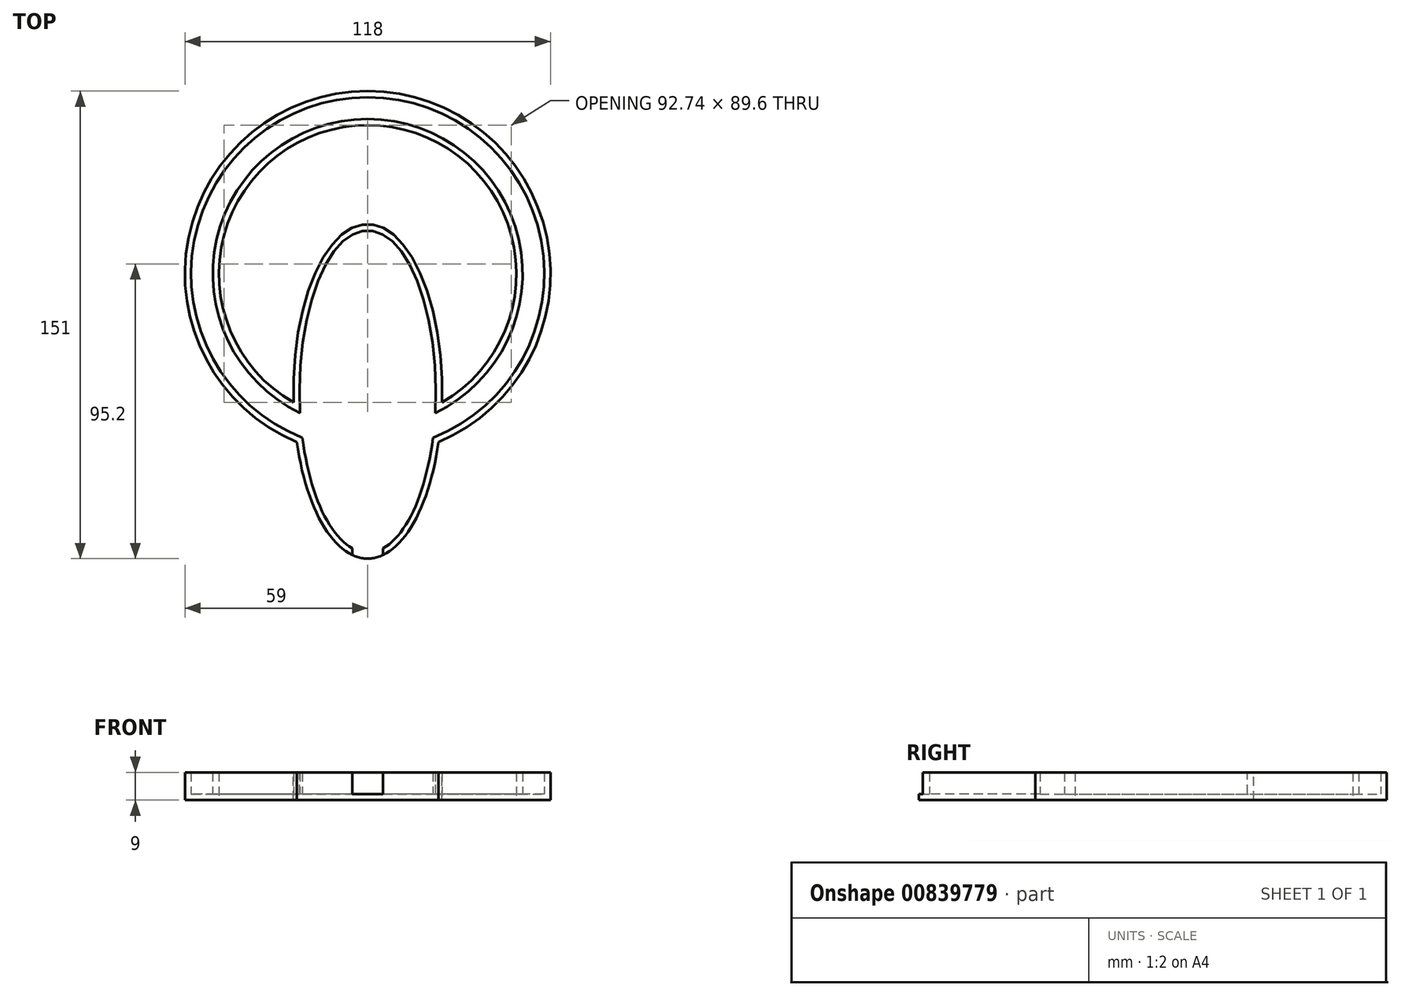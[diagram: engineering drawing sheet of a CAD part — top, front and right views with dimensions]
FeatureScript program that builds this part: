
annotation { "Feature Type Name" : "Feature", "Feature Type Description" : "" }
export const myFeature = defineFeature(function(context is Context, id is Id, definition is map)
    precondition{}
    {
        {
            var Q0;
            Q0=qCreatedBy(makeId("Top.planeOp"),FACE);
            var sketch = newSketch(context, id + "F0", { "sketchPlane" : qUnion([Q0])});
            skCircle(sketch, "E0", {"center": v(0, 0) * mm, "radius": 48 * mm});
            skCircle(sketch, "E1", {"center": v(0, 0) * mm, "radius": 50 * mm});
            skSolve(sketch);
        }
        {
            var Q0;
            Q0=makeQuery(id+"F0.imprint","IMPRINT",FACE,{"disambiguationData":[TD([[makeQuery(id+"F0.imprint","IMPRINT",EDGE,{"derivedFrom":sQuery(id+"F0.wireOp",EDGE,"E0")}),-1.0]])]});
            extrude(context, id + "F1", {"entities" : qUnion([Q0]), "depth" : 9 * mm, "offsetDistance" : 25 * mm});
        }
        {
            var Q0;
            Q0=qCreatedBy(makeId("Top.planeOp"),FACE);
            var sketch = newSketch(context, id + "F2", { "sketchPlane" : qUnion([Q0])});
            skCircle(sketch, "E2", {"center": v(0, 0) * mm, "radius": 50 * mm});
            skCircle(sketch, "E3", {"center": v(0, 0) * mm, "radius": 57 * mm});
            skSolve(sketch);
        }
        {
            var Q0;
            Q0=makeQuery(id+"F2.imprint","IMPRINT",FACE,{"disambiguationData":[TD([[makeQuery(id+"F2.imprint","IMPRINT",EDGE,{"derivedFrom":sQuery(id+"F2.wireOp",EDGE,"E2")}),-1.0]])]});
            extrude(context, id + "F3", {"entities" : qUnion([Q0]), "operationType" : NewBodyOperationType.ADD, "depth" : 2 * mm, "offsetDistance" : 25 * mm});
        }
        {
            var Q0;
            Q0=qCreatedBy(makeId("Top.planeOp"),FACE);
            var sketch = newSketch(context, id + "F4", { "sketchPlane" : qUnion([Q0])});
            skCircle(sketch, "E4", {"center": v(0, 0) * mm, "radius": 57 * mm});
            skCircle(sketch, "E5", {"center": v(0, 0) * mm, "radius": 59 * mm});
            skSolve(sketch);
        }
        {
            var Q0;
            Q0=makeQuery(id+"F4.imprint","IMPRINT",FACE,{"disambiguationData":[TD([[makeQuery(id+"F4.imprint","IMPRINT",EDGE,{"derivedFrom":sQuery(id+"F4.wireOp",EDGE,"E4")}),-1.0]])]});
            extrude(context, id + "F5", {"entities" : qUnion([Q0]), "operationType" : NewBodyOperationType.ADD, "depth" : 9 * mm, "offsetDistance" : 25 * mm});
        }
        {
            var Q0;
            Q0=qCreatedBy(makeId("Top.planeOp"),FACE);
            var sketch = newSketch(context, id + "F6", { "sketchPlane" : qUnion([Q0])});
            skEllipse(sketch, "E6", {"center": v(0, -38) * mm, "majorRadius": 52 * mm, "minorRadius": 22 * mm, "majorAxis": v(0, 1)});
            skEllipse(sketch, "E7", {"center": v(0, -38) * mm, "majorRadius": 54 * mm, "minorRadius": 24 * mm, "majorAxis": v(0, 1)});
            skSolve(sketch);
        }
        {
            var Q0;
            Q0=makeQuery(id+"F6.imprint","IMPRINT",FACE,{"disambiguationData":[TD([[makeQuery(id+"F6.imprint","IMPRINT",EDGE,{"derivedFrom":sQuery(id+"F6.wireOp",EDGE,"E6")}),-1.0]])]});
            extrude(context, id + "F7", {"entities" : qUnion([Q0]), "operationType" : NewBodyOperationType.ADD, "depth" : 9 * mm, "offsetDistance" : 25 * mm});
        }
        {
            var Q0;
            Q0=qCreatedBy(makeId("Top.planeOp"),FACE);
            var sketch = newSketch(context, id + "F8", { "sketchPlane" : qUnion([Q0])});
            skEllipse(sketch, "E8", {"center": v(0, -38) * mm, "majorRadius": 52 * mm, "minorRadius": 22 * mm, "majorAxis": v(0, 1)});
            skSolve(sketch);
        }
        {
            var Q0;
            Q0=makeQuery(id+"F8.imprint","IMPRINT",FACE,{"disambiguationData":[TD([[makeQuery(id+"F8.imprint","IMPRINT",EDGE,{"derivedFrom":sQuery(id+"F8.wireOp",EDGE,"E8")}),1.0]])]});
            extrude(context, id + "F9", {"entities" : qUnion([Q0]), "operationType" : NewBodyOperationType.ADD, "depth" : 2 * mm, "offsetDistance" : 25 * mm});
        }
        {
            var Q0;
            Q0=makeQuery(id+"F9.boolean.opBoolean","SPLIT",FACE,{"disambiguationData":[TD([makeQuery(id+"F1.opExtrude","SWEPT_FACE",FACE,{"disambiguationData":[OSD([sQuery(id+"F0.wireOp",EDGE,"E0")])]})])],"derivedFrom":makeQuery(id+"F9.opExtrude","CAP_FACE",FACE,{"disambiguationData":[OSD([sQuery(id+"F8.wireOp",EDGE,"E8")])],"isStart":false})});
            cPlane(context, id + "F10", {"entities" : qUnion([Q0]), "cplaneType" : CPlaneType.OFFSET, "offset" : 0 * mm, "width" : 150 * mm, "height" : 150 * mm});
        }
        {
            var Q0;
            Q0=qCreatedBy(id+"F10.planeOp",FACE);
            var sketch = newSketch(context, id + "F11", { "sketchPlane" : qUnion([Q0])});
            skCircle(sketch, "E9", {"center": v(0, 0) * mm, "radius": 50 * mm});
            skCircle(sketch, "E10", {"center": v(0, 0) * mm, "radius": 57 * mm});
            skSolve(sketch);
        }
        {
            var Q0;
            Q0=makeQuery(id+"F11.imprint","IMPRINT",FACE,{"disambiguationData":[TD([[makeQuery(id+"F11.imprint","IMPRINT",EDGE,{"derivedFrom":sQuery(id+"F11.wireOp",EDGE,"E9")}),-1.0]])]});
            extrude(context, id + "F12", {"entities" : qUnion([Q0]), "operationType" : NewBodyOperationType.REMOVE, "depth" : 7 * mm, "offsetDistance" : 25 * mm});
        }
        {
            var Q0;
            Q0=qCreatedBy(id+"F10.planeOp",FACE);
            var sketch = newSketch(context, id + "F13", { "sketchPlane" : qUnion([Q0])});
            skEllipse(sketch, "E11", {"center": v(0, -38) * mm, "majorRadius": 52 * mm, "minorRadius": 22 * mm, "majorAxis": v(0, 1)});
            skSolve(sketch);
        }
        {
            var Q0;
            Q0=makeQuery(id+"F13.imprint","IMPRINT",FACE,{"disambiguationData":[TD([[makeQuery(id+"F13.imprint","IMPRINT",EDGE,{"derivedFrom":sQuery(id+"F13.wireOp",EDGE,"E11")}),1.0]])]});
            extrude(context, id + "F14", {"entities" : qUnion([Q0]), "operationType" : NewBodyOperationType.REMOVE, "depth" : 7 * mm, "offsetDistance" : 25 * mm});
        }
        {
            var Q0;
            Q0=qCreatedBy(makeId("Front.planeOp"),FACE);
            var sketch = newSketch(context, id + "F15", { "sketchPlane" : qUnion([Q0])});
            skLineSegment(sketch, "E12.bottom", {"start": v(-5, 9) * mm, "end": v(5, 9) * mm});
            skLineSegment(sketch, "E12.top", {"start": v(-5, 2) * mm, "end": v(5, 2) * mm});
            skLineSegment(sketch, "E12.left", {"start": v(-5, 9) * mm, "end": v(-5, 2) * mm});
            skLineSegment(sketch, "E12.right", {"start": v(5, 9) * mm, "end": v(5, 2) * mm});
            skPoint(sketch, "E12.middle", {"position": v(0, 5.5) * mm});
            skSolve(sketch);
        }
        {
            var Q0;
            Q0=makeQuery(id+"F15.imprint","IMPRINT",FACE,{"disambiguationData":[TD([[makeQuery(id+"F15.imprint","IMPRINT",EDGE,{"derivedFrom":sQuery(id+"F15.wireOp",EDGE,"E12.bottom")}),-1.0]])]});
            extrude(context, id + "F16", {"entities" : qUnion([Q0]), "operationType" : NewBodyOperationType.REMOVE, "depth" : 100 * mm, "offsetDistance" : 25 * mm});
        }
    });
